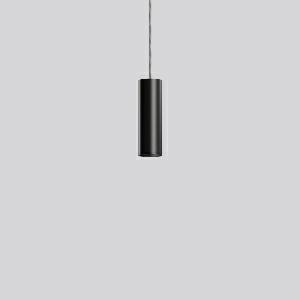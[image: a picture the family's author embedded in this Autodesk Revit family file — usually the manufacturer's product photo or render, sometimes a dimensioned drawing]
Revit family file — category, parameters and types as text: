
# Revit family: deecos_p_micro_911489_003_6a69
name_source: partatom
category: Lighting Fixtures
units: mm (PartAtom-declared; Revit-internal decimal feet)

## family parameters
Cut with Voids When Loaded = No
Host = Face
Light Source = No
Part Type = Normal
Room Calculation Point = No
Round Connector Dimension = Use Diameter
Shared = No

## types (1)
- DEECOS P micro (1 x LED Modul 927, 1600 lm, 2700)
    Apparent Load = 16 VA
    CIE Flux Codes = 98 100 100 100 100
    Color Rendering = 92
    Color Temperature = 2700
    Default Elevation = 1800 mm
    Description = Series: DEECOS P micro
Cylindrical pendant luminaire. Housing: die-cast aluminium, powder-coated. Canopy made of powder-coated sheet steel with magnetic attachment. Optical assembly with reflector made of MIRO-Silver with 98% total light reflection for outstanding efficiency - can be changed without tools. Black plastic ring and recessed LED to prevent glare from the side. Best colour rendering index Ra>90. Transparent suspension cable 3 m, can be shortened. High quality converter without flickering and stroboscopic effect. 
Colour: deep black, matt (RAL 9005)
Diameter: 60 mm
Height: 190 mm
Suspension length: 3000 mm
Lamp: LED
Socket: without socket
Colour temperature: 2700K
Colour rendering index (CRI): 92
System power: 16 W
Rated luminous flux: 1600 lm
Luminous efficiency: 100 lm/W
Control gear: Regulated power supply
Protection class: I
Type of protection: IP 20
    Height = 190 mm  [stored 0.62336 ft]
    Lamp = 1 x LED Modul 927
    Lamp Light Flux = 1600 lm
    Lamp count = 1
    Length = 60 mm  [stored 0.19685 ft]
    Lifetime = 50000 h
    Luminous efficacy = 100 lm/W
    Manufacturer = RZB
    ModVariant = No
    Model = 911489.003
    Mounting Place = Ceiling
    Mounting Type = Pendant
    Number of Poles = 1
    OnlyDefault = Yes
    Power Factor = 1
    Product Name = DEECOS P micro
    Product group = Pendant luminaires
    ProductGroupID = 902
    Protection Class = Protection class I
    Protection Degree = Degree of protection
    RLX_Detail_Level = 1
    RLX_Emergency_Light_Flux = 0 lm
    RLX_Emergency_Type = 0
    RLX_Emergency_Type_DB = No
    RlxData = <blob elided: 31789 chars, md5=c2811243>
    Socket = socket
    Standby Power = 0 W
    System Light Flux = 1600 lm
    System Power = 16 W
    Type Comments = Product without accessories
    Type Image = 911489.003.jpg
    URL = http://relux.com
    VarID = ---
    Voltage = 0 V
    Weight = 0.00 kg
    Width = 0 mm  [stored 0 ft]

note: [stored X ft] marks values corroborated as IEEE doubles in the binary element streams (Revit-internal decimal feet)

## geometry (parser evidence)
native form markers: Blend x4, Sweep x10
no freeform markers — native parametric forms only
